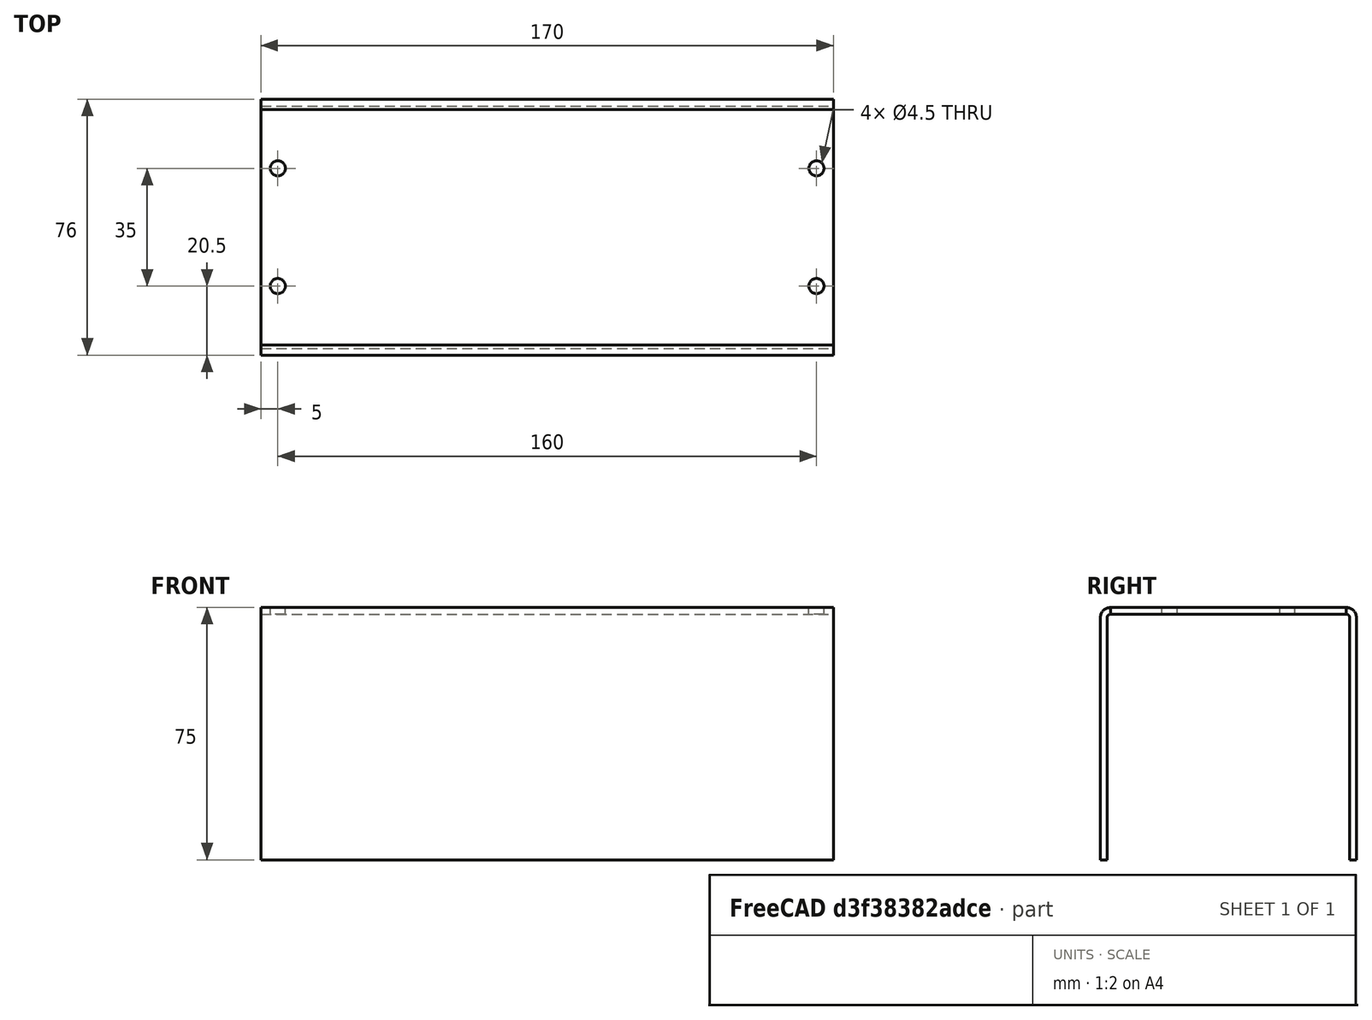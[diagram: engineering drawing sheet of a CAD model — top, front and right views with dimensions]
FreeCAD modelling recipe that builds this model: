
FCSTD DOCUMENT  (FreeCAD 0.17R11624 (Git))
Label: cover_top
License: All rights reserved
LicenseURL: http://en.wikipedia.org/wiki/All_rights_reserved
objects: Part::Cylinder×4, Part::Cut×4, Part::FeaturePython×2, Part::Box×1
note: 11 computed .brp shape members not serialized (recipe doc carries the construction recipe); baked Part::Feature solids carry a one-line shape summary decoded from their .brp

FEATURE [Part::Box] Box  label="Base Flange"
  AttacherType = Attacher::AttachEngine3D
  Height = 2
  Length = 170
  Width = 70
FEATURE [Part::FeaturePython] Bend  label="Front Wall"  # WARN: FeaturePython — macro-defined, semantics opaque (R4)
  angle = 90
  baseObject = -> Box [Face3]
  gap1 = 0
  gap2 = 0
  invert = true
  length = 72
  radius = 1
  reliefd = 1
  reliefw = 0.5
FEATURE [Part::FeaturePython] Bend001  label="Back Wall"  # WARN: FeaturePython — macro-defined, semantics opaque (R4)
  angle = 90
  baseObject = -> Bend [Face14]
  gap1 = 0
  gap2 = 0
  invert = true
  length = 72
  radius = 1
  reliefd = 1
  reliefw = 0.5
FEATURE [Part::Cylinder] Cylinder001  label="Top Hole Tool 1"
  Angle = 360
  AttacherType = Attacher::AttachEngine3D
  Height = 2
  Placement = pos=(5,17.5,0) rot=(0,0,1;0rad)
  Radius = 2.25
FEATURE [Part::Cut] Cut001
  Base = -> Bend001
  Tool = -> Cylinder001
FEATURE [Part::Cylinder] Cylinder002  label="Top Hole Tool 2"
  Angle = 360
  AttacherType = Attacher::AttachEngine3D
  Height = 2
  Placement = pos=(5,52.5,0) rot=(0,0,1;0rad)
  Radius = 2.25
FEATURE [Part::Cut] Cut002
  Base = -> Cut001
  Tool = -> Cylinder002
FEATURE [Part::Cylinder] Cylinder003  label="Top Hole Tool 3"
  Angle = 360
  AttacherType = Attacher::AttachEngine3D
  Height = 2
  Placement = pos=(165,17.5,0) rot=(0,0,1;0rad)
  Radius = 2.25
FEATURE [Part::Cut] Cut003
  Base = -> Cut002
  Tool = -> Cylinder003
FEATURE [Part::Cylinder] Cylinder004  label="Cover Bottom Mount"
  Angle = 360
  AttacherType = Attacher::AttachEngine3D
  Height = 2
  Placement = pos=(165,52.5,0) rot=(0,0,1;0rad)
  Radius = 2.25
FEATURE [Part::Cut] Cut004
  Base = -> Cut003
  Tool = -> Cylinder004
